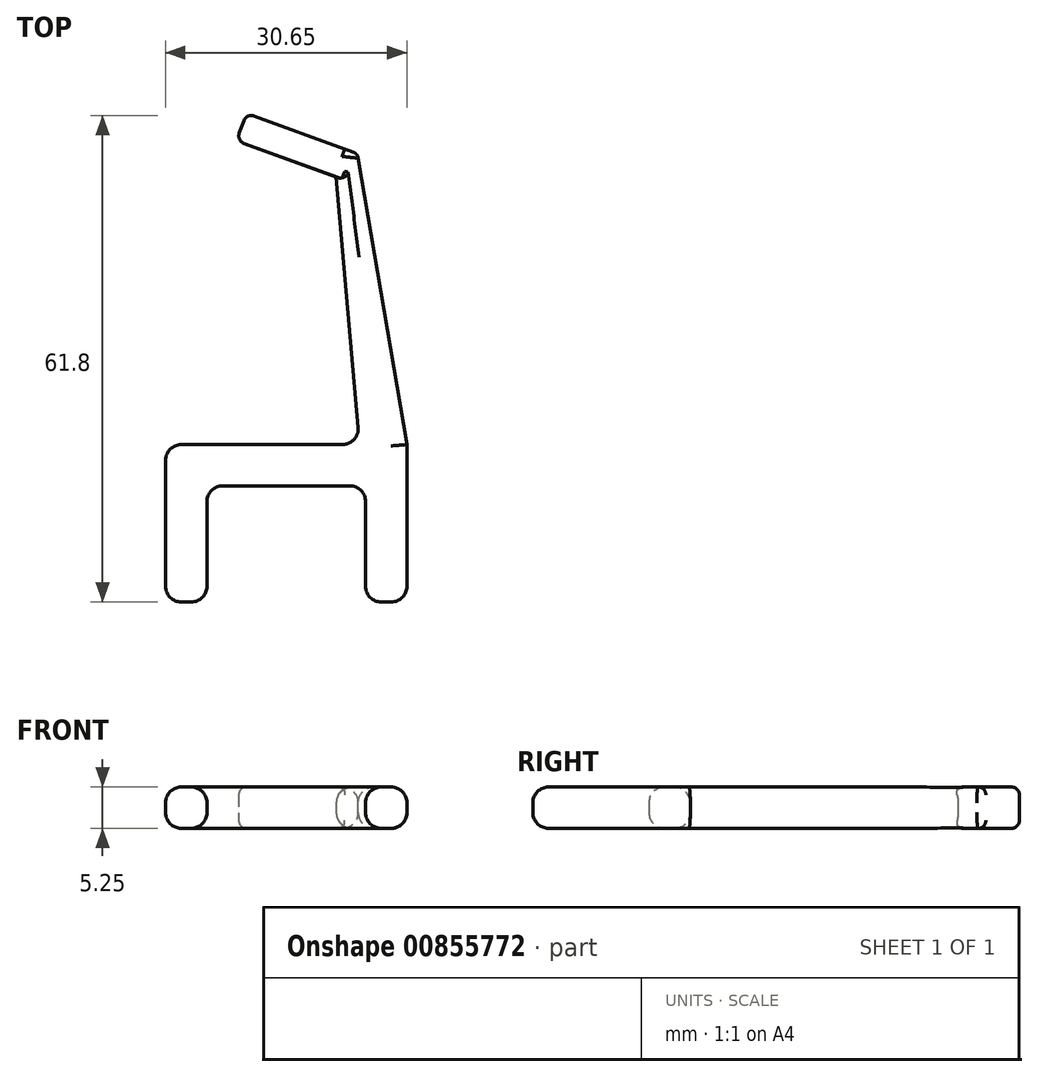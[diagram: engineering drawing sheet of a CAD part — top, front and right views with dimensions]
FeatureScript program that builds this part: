
annotation { "Feature Type Name" : "Feature", "Feature Type Description" : "" }
export const myFeature = defineFeature(function(context is Context, id is Id, definition is map)
    precondition{}
    {
        {
            var Q0;
            Q0=qCreatedBy(makeId("Top.planeOp"),FACE);
            var sketch = newSketch(context, id + "F0", { "sketchPlane" : qUnion([Q0])});
            skLineSegment(sketch, "E0", {"start": v(0, 0) * mm, "end": v(0, 20) * mm});
            skLineSegment(sketch, "E1", {"start": v(0, 20) * mm, "end": v(24.65, 20) * mm});
            skLineSegment(sketch, "E2", {"start": v(24.65, 20) * mm, "end": v(21.68, 54) * mm});
            skLineSegment(sketch, "E3", {"start": v(21.68, 54) * mm, "end": v(9.01, 58.6) * mm});
            skLineSegment(sketch, "E4", {"start": v(9.01, 58.6) * mm, "end": v(10.28, 62.09) * mm});
            skLineSegment(sketch, "E5", {"start": v(10.28, 62.09) * mm, "end": v(24.37, 56.95) * mm});
            skLineSegment(sketch, "E6", {"start": v(30.65, 0) * mm, "end": v(25.4, 0) * mm});
            skLineSegment(sketch, "E7", {"start": v(25.4, 0) * mm, "end": v(25.4, 14.75) * mm});
            skLineSegment(sketch, "E8", {"start": v(25.4, 14.75) * mm, "end": v(5.25, 14.75) * mm});
            skLineSegment(sketch, "E9", {"start": v(5.25, 14.75) * mm, "end": v(5.25, 0) * mm});
            skLineSegment(sketch, "E10", {"start": v(5.25, 0) * mm, "end": v(0, 0) * mm});
            skLineSegment(sketch, "E11", {"start": v(30.65, 0) * mm, "end": v(30.65, 20) * mm});
            skLineSegment(sketch, "E12", {"start": v(30.65, 20) * mm, "end": v(24.37, 56.95) * mm});
            skSolve(sketch);
        }
        {
            var Q0;
            Q0=makeQuery(id+"F0.imprint","IMPRINT",FACE,{"disambiguationData":[TD([[makeQuery(id+"F0.imprint","IMPRINT",EDGE,{"derivedFrom":sQuery(id+"F0.wireOp",EDGE,"E0")}),-1.0]])]});
            extrude(context, id + "F1", {"entities" : qUnion([Q0]), "depth" : 5.25 * mm, "offsetDistance" : 25.4 * mm});
        }
        {
            var Q0;
            Q0=makeQuery(id+"F1.opExtrude","SWEPT_FACE",FACE,{"disambiguationData":[OSD([sQuery(id+"F0.wireOp",EDGE,"E6")])]});
            var Q1;
            Q1=makeQuery(id+"F1.opExtrude","SWEPT_FACE",FACE,{"disambiguationData":[OSD([sQuery(id+"F0.wireOp",EDGE,"E10")])]});
            var Q2;
            Q2=makeQuery(id+"F1.opExtrude","CAP_EDGE",EDGE,{"disambiguationData":[OSD([sQuery(id+"F0.wireOp",EDGE,"E7")])],"isStart":false});
            var Q3;
            Q3=makeQuery(id+"F1.opExtrude","CAP_EDGE",EDGE,{"disambiguationData":[OSD([sQuery(id+"F0.wireOp",EDGE,"E11")])],"isStart":false});
            var Q4;
            Q4=makeQuery(id+"F1.opExtrude","CAP_EDGE",EDGE,{"disambiguationData":[OSD([sQuery(id+"F0.wireOp",EDGE,"E11")])],"isStart":true});
            var Q5;
            Q5=makeQuery(id+"F1.opExtrude","CAP_EDGE",EDGE,{"disambiguationData":[OSD([sQuery(id+"F0.wireOp",EDGE,"E12")])],"isStart":false});
            var Q6;
            Q6=makeQuery(id+"F1.opExtrude","CAP_EDGE",EDGE,{"disambiguationData":[OSD([sQuery(id+"F0.wireOp",EDGE,"E2")])],"isStart":false});
            var Q7;
            Q7=makeQuery(id+"F1.opExtrude","CAP_EDGE",EDGE,{"disambiguationData":[OSD([sQuery(id+"F0.wireOp",EDGE,"E2")])],"isStart":true});
            var Q8;
            Q8=makeQuery(id+"F1.opExtrude","CAP_EDGE",EDGE,{"disambiguationData":[OSD([sQuery(id+"F0.wireOp",EDGE,"E12")])],"isStart":true});
            var Q9;
            Q9=makeQuery(id+"F1.opExtrude","CAP_EDGE",EDGE,{"disambiguationData":[OSD([sQuery(id+"F0.wireOp",EDGE,"E8")])],"isStart":true});
            var Q10;
            Q10=makeQuery(id+"F1.opExtrude","CAP_EDGE",EDGE,{"disambiguationData":[OSD([sQuery(id+"F0.wireOp",EDGE,"E1")])],"isStart":true});
            var Q11;
            Q11=makeQuery(id+"F1.opExtrude","CAP_EDGE",EDGE,{"disambiguationData":[OSD([sQuery(id+"F0.wireOp",EDGE,"E9")])],"isStart":true});
            var Q12;
            Q12=makeQuery(id+"F1.opExtrude","CAP_EDGE",EDGE,{"disambiguationData":[OSD([sQuery(id+"F0.wireOp",EDGE,"E0")])],"isStart":true});
            var Q13;
            Q13=makeQuery(id+"F1.opExtrude","CAP_EDGE",EDGE,{"disambiguationData":[OSD([sQuery(id+"F0.wireOp",EDGE,"E0")])],"isStart":false});
            var Q14;
            Q14=makeQuery(id+"F1.opExtrude","CAP_EDGE",EDGE,{"disambiguationData":[OSD([sQuery(id+"F0.wireOp",EDGE,"E8")])],"isStart":false});
            var Q15;
            Q15=makeQuery(id+"F1.opExtrude","CAP_EDGE",EDGE,{"disambiguationData":[OSD([sQuery(id+"F0.wireOp",EDGE,"E7")])],"isStart":true});
            var Q16;
            Q16=makeQuery(id+"F1.opExtrude","CAP_EDGE",EDGE,{"disambiguationData":[OSD([sQuery(id+"F0.wireOp",EDGE,"E9")])],"isStart":false});
            var Q17;
            Q17=makeQuery(id+"F1.opExtrude","CAP_EDGE",EDGE,{"disambiguationData":[OSD([sQuery(id+"F0.wireOp",EDGE,"E1")])],"isStart":false});
            var Q18;
            Q18=makeQuery(id+"F1.opExtrude","SWEPT_EDGE",EDGE,{"disambiguationData":[OSD([sQuery(id+"F0.wireOp",EDGE,"E1"),sQuery(id+"F0.wireOp",EDGE,"E2")])]});
            var Q19;
            Q19=makeQuery(id+"F1.opExtrude","SWEPT_EDGE",EDGE,{"disambiguationData":[OSD([sQuery(id+"F0.wireOp",EDGE,"E7"),sQuery(id+"F0.wireOp",EDGE,"E8")])]});
            var Q20;
            Q20=makeQuery(id+"F1.opExtrude","SWEPT_EDGE",EDGE,{"disambiguationData":[OSD([sQuery(id+"F0.wireOp",EDGE,"E8"),sQuery(id+"F0.wireOp",EDGE,"E9")])]});
            var Q21;
            Q21=makeQuery(id+"F1.opExtrude","SWEPT_EDGE",EDGE,{"disambiguationData":[OSD([sQuery(id+"F0.wireOp",EDGE,"E0"),sQuery(id+"F0.wireOp",EDGE,"E1")])]});
            fillet(context, id + "F2", {"entities" : qUnion([Q0, Q1, Q2, Q3, Q4, Q5, Q6, Q7, Q8, Q9, Q10, Q11, Q12, Q13, Q14, Q15, Q16, Q17, Q18, Q19, Q20, Q21]), "radius" : 2 * mm, "tangentPropagation" : true, "allowEdgeOverflow" : false});
        }
        {
            var Q0;
            Q0=makeQuery(id+"F1.opExtrude","SWEPT_FACE",FACE,{"disambiguationData":[OSD([sQuery(id+"F0.wireOp",EDGE,"E4")])]});
            var Q1;
            Q1=makeQuery(id+"F1.opExtrude","CAP_EDGE",EDGE,{"disambiguationData":[OSD([sQuery(id+"F0.wireOp",EDGE,"E3")])],"isStart":false});
            var Q2;
            Q2=makeQuery(id+"F1.opExtrude","CAP_EDGE",EDGE,{"disambiguationData":[OSD([sQuery(id+"F0.wireOp",EDGE,"E3")])],"isStart":true});
            var Q3;
            Q3=makeQuery(id+"F1.opExtrude","SWEPT_EDGE",EDGE,{"disambiguationData":[OSD([sQuery(id+"F0.wireOp",EDGE,"E5"),sQuery(id+"F0.wireOp",EDGE,"E12")])]});
            fillet(context, id + "F3", {"entities" : qUnion([Q0, Q1, Q2, Q3]), "radius" : 1 * mm, "tangentPropagation" : true, "allowEdgeOverflow" : false});
        }
    });
